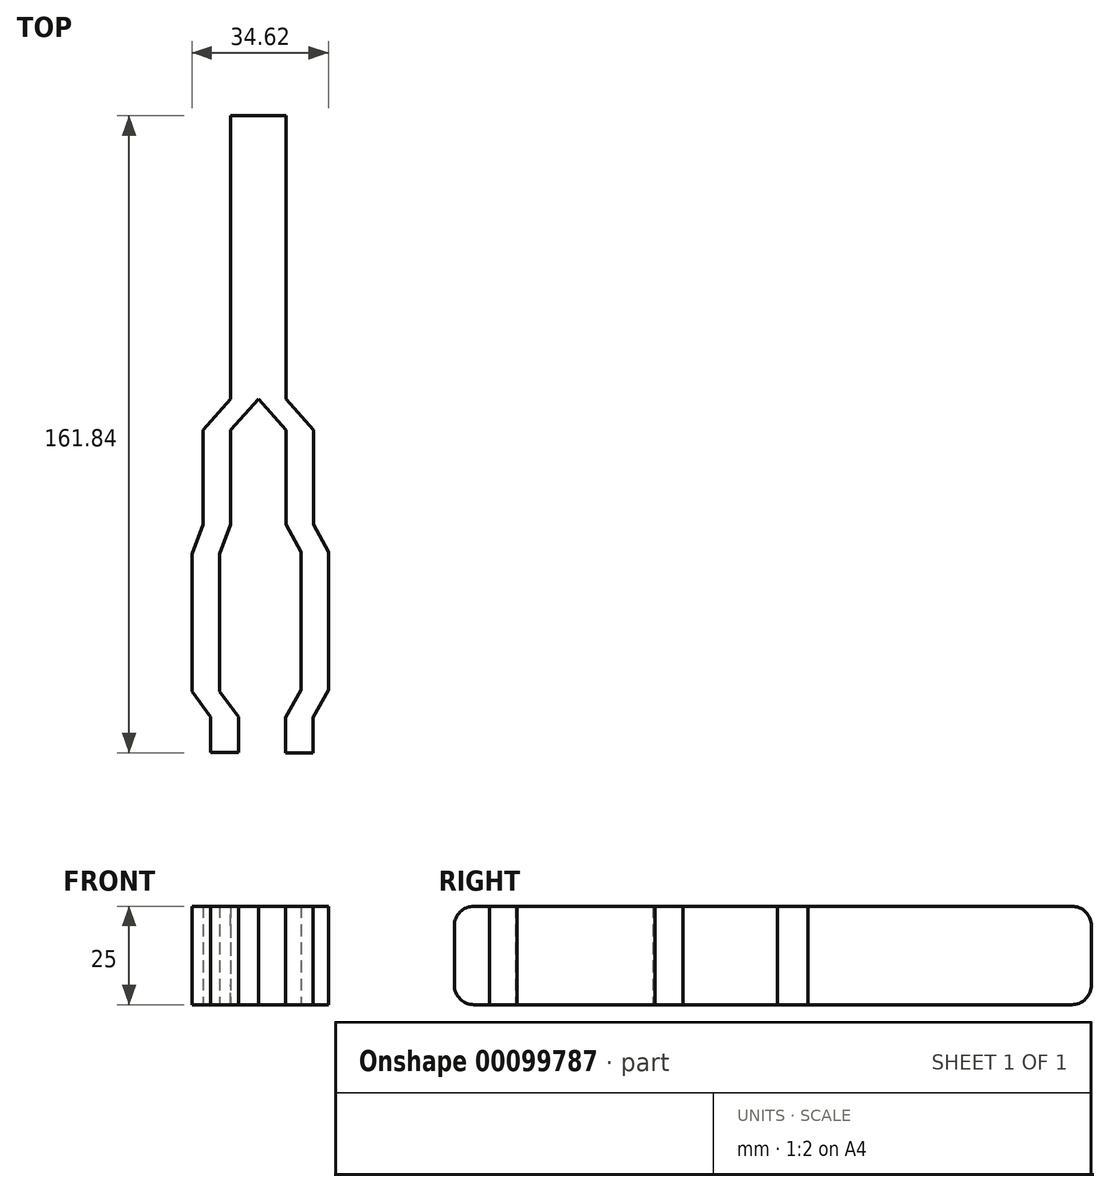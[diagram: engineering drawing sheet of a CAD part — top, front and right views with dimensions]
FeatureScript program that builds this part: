
annotation { "Feature Type Name" : "Feature", "Feature Type Description" : "" }
export const myFeature = defineFeature(function(context is Context, id is Id, definition is map)
    precondition{}
    {
        {
            var Q0;
            Q0=qCreatedBy(makeId("Top.planeOp"),FACE);
            var sketch = newSketch(context, id + "F0", { "sketchPlane" : qUnion([Q0])});
            skLineSegment(sketch, "E0", {"start": v(-7.03, 72) * mm, "end": v(-7.03, 0) * mm});
            skLineSegment(sketch, "E1", {"start": v(-7.03, 0) * mm, "end": v(-14.06, -7.82) * mm});
            skLineSegment(sketch, "E2", {"start": v(-14.06, -7.82) * mm, "end": v(-14.06, -31.82) * mm});
            skLineSegment(sketch, "E3", {"start": v(-14.06, -31.82) * mm, "end": v(-16.85, -39.32) * mm});
            skLineSegment(sketch, "E4", {"start": v(-16.85, -39.32) * mm, "end": v(-16.85, -74.32) * mm});
            skLineSegment(sketch, "E5", {"start": v(-16.85, -74.32) * mm, "end": v(-12.1, -80.76) * mm});
            skLineSegment(sketch, "E6", {"start": v(-12.1, -80.76) * mm, "end": v(-12.1, -89.76) * mm});
            skLineSegment(sketch, "E7", {"start": v(-7.03, 72) * mm, "end": v(6.97, 72) * mm});
            skLineSegment(sketch, "E8", {"start": v(6.97, 72) * mm, "end": v(6.97, 0) * mm});
            skLineSegment(sketch, "E9", {"start": v(0, 0) * mm, "end": v(-7.03, -7.82) * mm});
            skLineSegment(sketch, "E10", {"start": v(-7.03, -7.82) * mm, "end": v(-7.03, -31.82) * mm});
            skLineSegment(sketch, "E11", {"start": v(-7.03, -31.82) * mm, "end": v(-9.82, -39.32) * mm});
            skLineSegment(sketch, "E12", {"start": v(-9.82, -39.32) * mm, "end": v(-9.82, -74.32) * mm});
            skLineSegment(sketch, "E13", {"start": v(-9.82, -74.32) * mm, "end": v(-5.07, -80.76) * mm});
            skLineSegment(sketch, "E14", {"start": v(-5.07, -80.76) * mm, "end": v(-5.07, -89.76) * mm});
            skLineSegment(sketch, "E15", {"start": v(-5.07, -89.76) * mm, "end": v(-12.1, -89.76) * mm});
            skLineSegment(sketch, "E16", {"start": v(0, 0) * mm, "end": v(7.06, -7.8) * mm});
            skLineSegment(sketch, "E17", {"start": v(7.06, -7.8) * mm, "end": v(7.06, -31.8) * mm});
            skLineSegment(sketch, "E18", {"start": v(7.06, -31.8) * mm, "end": v(10.8, -38.87) * mm});
            skLineSegment(sketch, "E19", {"start": v(10.8, -38.87) * mm, "end": v(10.8, -73.87) * mm});
            skLineSegment(sketch, "E20", {"start": v(10.8, -73.87) * mm, "end": v(6.88, -80.84) * mm});
            skLineSegment(sketch, "E21", {"start": v(6.88, -80.84) * mm, "end": v(6.88, -89.84) * mm});
            skLineSegment(sketch, "E22", {"start": v(6.88, -89.84) * mm, "end": v(13.85, -89.84) * mm});
            skLineSegment(sketch, "E23", {"start": v(13.85, -89.84) * mm, "end": v(13.85, -80.84) * mm});
            skLineSegment(sketch, "E24", {"start": v(13.85, -80.84) * mm, "end": v(17.77, -73.87) * mm});
            skLineSegment(sketch, "E25", {"start": v(17.77, -73.87) * mm, "end": v(17.77, -38.87) * mm});
            skLineSegment(sketch, "E26", {"start": v(17.77, -38.87) * mm, "end": v(14.03, -31.8) * mm});
            skLineSegment(sketch, "E27", {"start": v(14.03, -31.8) * mm, "end": v(14.03, -7.8) * mm});
            skLineSegment(sketch, "E28", {"start": v(14.03, -7.8) * mm, "end": v(6.97, 0) * mm});
            skSolve(sketch);
        }
        {
            var Q0;
            Q0=makeQuery(id+"F0.imprint","IMPRINT",FACE,{"disambiguationData":[TD([[makeQuery(id+"F0.imprint","IMPRINT",EDGE,{"derivedFrom":sQuery(id+"F0.wireOp",EDGE,"E0")}),1.0]])]});
            extrude(context, id + "F1", {"entities" : qUnion([Q0]), "depth" : 25 * mm});
        }
        {
            var Q0;
            Q0=makeQuery(id+"F1.opExtrude","CAP_EDGE",EDGE,{"disambiguationData":[OSD([sQuery(id+"F0.wireOp",EDGE,"E7")])],"isStart":false});
            var Q1;
            Q1=makeQuery(id+"F1.opExtrude","CAP_EDGE",EDGE,{"disambiguationData":[OSD([sQuery(id+"F0.wireOp",EDGE,"E7")])],"isStart":true});
            var Q2;
            Q2=makeQuery(id+"F1.opExtrude","CAP_EDGE",EDGE,{"disambiguationData":[OSD([sQuery(id+"F0.wireOp",EDGE,"E15")])],"isStart":true});
            var Q3;
            Q3=makeQuery(id+"F1.opExtrude","CAP_EDGE",EDGE,{"disambiguationData":[OSD([sQuery(id+"F0.wireOp",EDGE,"E22")])],"isStart":true});
            var Q4;
            Q4=makeQuery(id+"F1.opExtrude","CAP_EDGE",EDGE,{"disambiguationData":[OSD([sQuery(id+"F0.wireOp",EDGE,"E15")])],"isStart":false});
            var Q5;
            Q5=makeQuery(id+"F1.opExtrude","CAP_EDGE",EDGE,{"disambiguationData":[OSD([sQuery(id+"F0.wireOp",EDGE,"E22")])],"isStart":false});
            fillet(context, id + "F2", {"entities" : qUnion([Q0, Q1, Q2, Q3, Q4, Q5]), "radius" : 5 * mm, "tangentPropagation" : true, "allowEdgeOverflow" : false});
        }
    });
